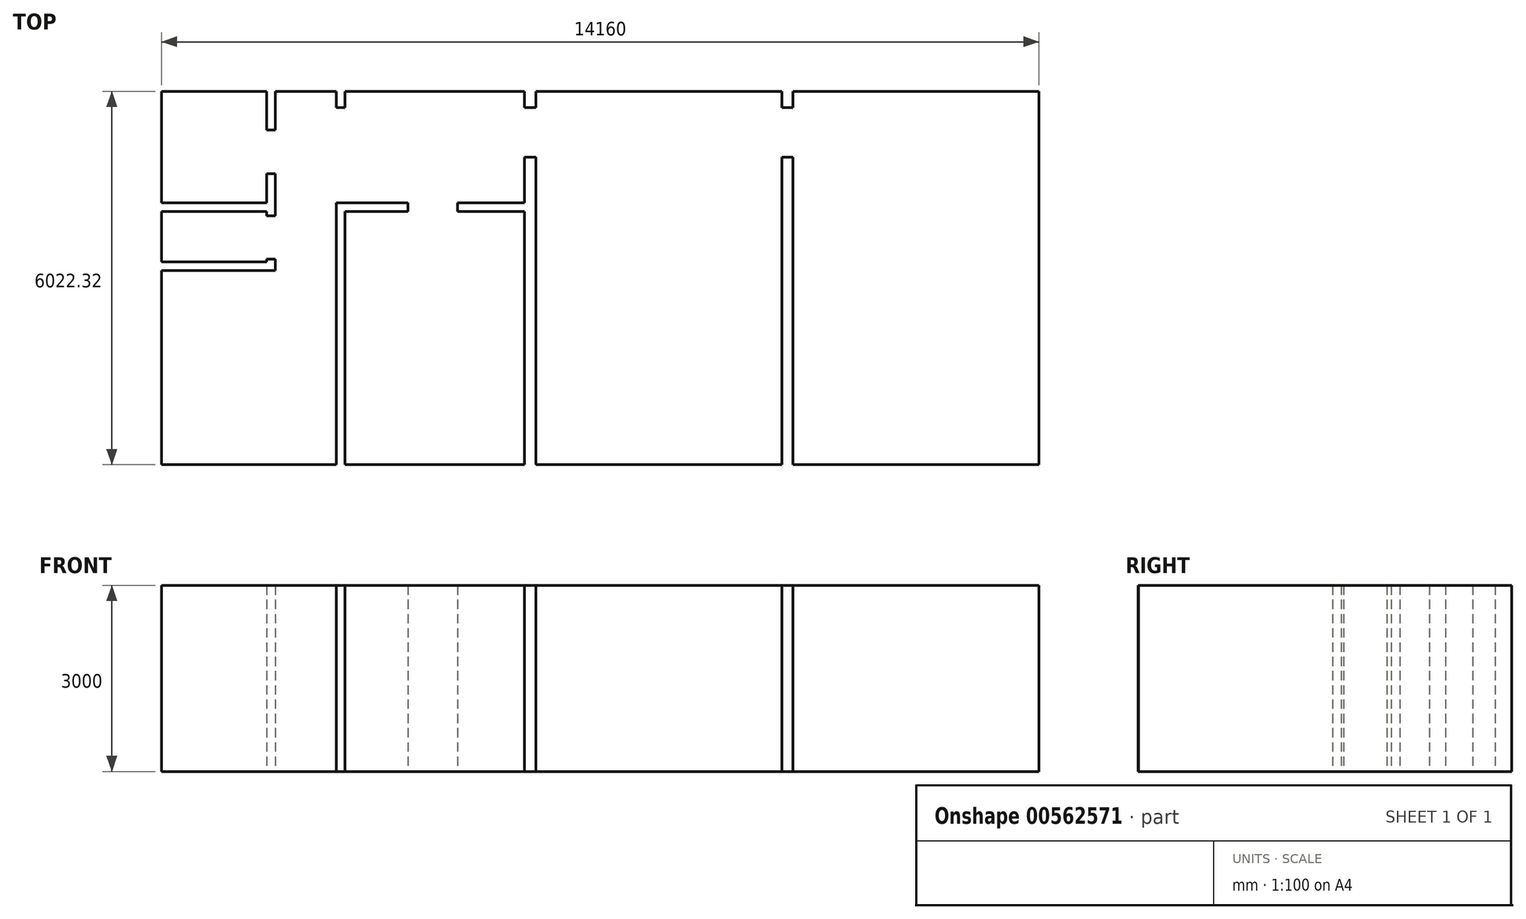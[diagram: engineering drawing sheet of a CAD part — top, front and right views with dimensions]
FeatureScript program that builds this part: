
annotation { "Feature Type Name" : "Feature", "Feature Type Description" : "" }
export const myFeature = defineFeature(function(context is Context, id is Id, definition is map)
    precondition{}
    {
        {
            var Q0;
            Q0=qCreatedBy(makeId("Top.planeOp"),FACE);
            var sketch = newSketch(context, id + "F0", { "sketchPlane" : qUnion([Q0])});
            skLineSegment(sketch, "E0", {"start": v(-548.5, 539.05) * mm, "end": v(-548.5, 3669.05) * mm});
            skLineSegment(sketch, "E1", {"start": v(-548.5, 3669.05) * mm, "end": v(1291.5, 3669.05) * mm});
            skLineSegment(sketch, "E2", {"start": v(1291.5, 3669.05) * mm, "end": v(1291.5, 3849.64) * mm});
            skLineSegment(sketch, "E3", {"start": v(1291.5, 3849.64) * mm, "end": v(1151.5, 3849.64) * mm});
            skLineSegment(sketch, "E4", {"start": v(1151.5, 3849.64) * mm, "end": v(1151.5, 3809.05) * mm});
            skLineSegment(sketch, "E5", {"start": v(1151.5, 3809.05) * mm, "end": v(-548.5, 3809.05) * mm});
            skLineSegment(sketch, "E6", {"start": v(-548.5, 3809.05) * mm, "end": v(-548.5, 4619.05) * mm});
            skLineSegment(sketch, "E7", {"start": v(-548.5, 4619.05) * mm, "end": v(1151.5, 4619.05) * mm});
            skLineSegment(sketch, "E8", {"start": v(1151.5, 4619.05) * mm, "end": v(1151.5, 4619.05) * mm});
            skLineSegment(sketch, "E9", {"start": v(1291.5, 4619.05) * mm, "end": v(1291.5, 5232.33) * mm});
            skLineSegment(sketch, "E10", {"start": v(1291.5, 5232.33) * mm, "end": v(1151.5, 5232.33) * mm});
            skLineSegment(sketch, "E11", {"start": v(1151.5, 5232.33) * mm, "end": v(1151.5, 4759.05) * mm});
            skLineSegment(sketch, "E12", {"start": v(1151.5, 4759.05) * mm, "end": v(-548.5, 4759.05) * mm});
            skLineSegment(sketch, "E13", {"start": v(-548.5, 4759.05) * mm, "end": v(-548.5, 6559.05) * mm});
            skLineSegment(sketch, "E14", {"start": v(-548.5, 6559.05) * mm, "end": v(1151.5, 6559.05) * mm});
            skLineSegment(sketch, "E15", {"start": v(1151.5, 6559.05) * mm, "end": v(1151.5, 5932.33) * mm});
            skLineSegment(sketch, "E16", {"start": v(1151.5, 5932.33) * mm, "end": v(1291.5, 5932.33) * mm});
            skLineSegment(sketch, "E17", {"start": v(1291.5, 5932.33) * mm, "end": v(1291.5, 6559.05) * mm});
            skLineSegment(sketch, "E18", {"start": v(1291.5, 6559.05) * mm, "end": v(2271.5, 6559.05) * mm});
            skLineSegment(sketch, "E19", {"start": v(2271.5, 6559.05) * mm, "end": v(2271.5, 6295.6) * mm});
            skLineSegment(sketch, "E20", {"start": v(2271.5, 6295.6) * mm, "end": v(2411.5, 6295.6) * mm});
            skLineSegment(sketch, "E21", {"start": v(2411.5, 6295.6) * mm, "end": v(2411.5, 6559.05) * mm});
            skLineSegment(sketch, "E22", {"start": v(2411.5, 6559.05) * mm, "end": v(5311.5, 6559.05) * mm});
            skLineSegment(sketch, "E23", {"start": v(5311.5, 6559.05) * mm, "end": v(5311.5, 6295.6) * mm});
            skLineSegment(sketch, "E24", {"start": v(5311.5, 6295.6) * mm, "end": v(5491.5, 6295.6) * mm});
            skLineSegment(sketch, "E25", {"start": v(5491.5, 6295.6) * mm, "end": v(5491.5, 6559.05) * mm});
            skLineSegment(sketch, "E26", {"start": v(5491.5, 6559.05) * mm, "end": v(9461.5, 6559.05) * mm});
            skLineSegment(sketch, "E27", {"start": v(9461.5, 6559.05) * mm, "end": v(9461.5, 6295.6) * mm});
            skLineSegment(sketch, "E28", {"start": v(9461.5, 6295.6) * mm, "end": v(9641.5, 6295.6) * mm});
            skLineSegment(sketch, "E29", {"start": v(9641.5, 6295.6) * mm, "end": v(9641.5, 6559.05) * mm});
            skLineSegment(sketch, "E30", {"start": v(9641.5, 6559.05) * mm, "end": v(13611.5, 6559.05) * mm});
            skLineSegment(sketch, "E31", {"start": v(13611.5, 6559.05) * mm, "end": v(13611.5, 539.05) * mm});
            skLineSegment(sketch, "E32", {"start": v(13611.5, 539.05) * mm, "end": v(9641.5, 539.05) * mm});
            skLineSegment(sketch, "E33", {"start": v(9641.5, 539.05) * mm, "end": v(9641.5, 5495.6) * mm});
            skLineSegment(sketch, "E34", {"start": v(9641.5, 5495.6) * mm, "end": v(9461.5, 5495.6) * mm});
            skLineSegment(sketch, "E35", {"start": v(9461.5, 5495.6) * mm, "end": v(9461.5, 539.05) * mm});
            skLineSegment(sketch, "E36", {"start": v(9461.5, 539.05) * mm, "end": v(5491.5, 539.05) * mm});
            skLineSegment(sketch, "E37", {"start": v(5491.5, 539.05) * mm, "end": v(5491.5, 5495.6) * mm});
            skLineSegment(sketch, "E38", {"start": v(5491.5, 5495.6) * mm, "end": v(5311.5, 5495.6) * mm});
            skLineSegment(sketch, "E39", {"start": v(5311.5, 5495.6) * mm, "end": v(5311.5, 4759.05) * mm});
            skLineSegment(sketch, "E40", {"start": v(5311.5, 539.05) * mm, "end": v(2411.5, 536.73) * mm});
            skLineSegment(sketch, "E41", {"start": v(2411.5, 536.73) * mm, "end": v(2411.5, 4619.05) * mm});
            skLineSegment(sketch, "E42", {"start": v(2411.5, 4619.05) * mm, "end": v(3432.49, 4619.05) * mm});
            skLineSegment(sketch, "E43", {"start": v(3432.49, 4619.05) * mm, "end": v(3432.49, 4759.05) * mm});
            skLineSegment(sketch, "E44", {"start": v(3432.49, 4759.05) * mm, "end": v(2271.5, 4759.05) * mm});
            skLineSegment(sketch, "E45", {"start": v(2271.5, 4759.05) * mm, "end": v(2271.5, 536.73) * mm});
            skLineSegment(sketch, "E46", {"start": v(2271.5, 536.73) * mm, "end": v(-548.5, 539.05) * mm});
            skLineSegment(sketch, "E47", {"start": v(5311.5, 4759.05) * mm, "end": v(4232.49, 4759.05) * mm});
            skLineSegment(sketch, "E48", {"start": v(4232.49, 4759.05) * mm, "end": v(4232.49, 4619.05) * mm});
            skLineSegment(sketch, "E49", {"start": v(4232.49, 4619.05) * mm, "end": v(5311.5, 4619.05) * mm});
            skLineSegment(sketch, "E50.trimOffspring", {"start": v(5311.5, 4619.05) * mm, "end": v(5311.5, 539.05) * mm});
            skLineSegment(sketch, "E51", {"start": v(1151.5, 4619.05) * mm, "end": v(1151.5, 4549.64) * mm});
            skLineSegment(sketch, "E52", {"start": v(1151.5, 4549.64) * mm, "end": v(1291.5, 4549.64) * mm});
            skLineSegment(sketch, "E53", {"start": v(1291.5, 4549.64) * mm, "end": v(1291.5, 4619.05) * mm});
            skSolve(sketch);
        }
        {
            var Q0;
            Q0=makeQuery(id+"F0.imprint","IMPRINT",FACE,{"disambiguationData":[TD([[makeQuery(id+"F0.imprint","IMPRINT",EDGE,{"derivedFrom":sQuery(id+"F0.wireOp",EDGE,"E0")}),-1.0]])]});
            extrude(context, id + "F1", {"entities" : qUnion([Q0]), "depth" : 3000 * mm, "offsetDistance" : 25 * mm});
        }
    });
